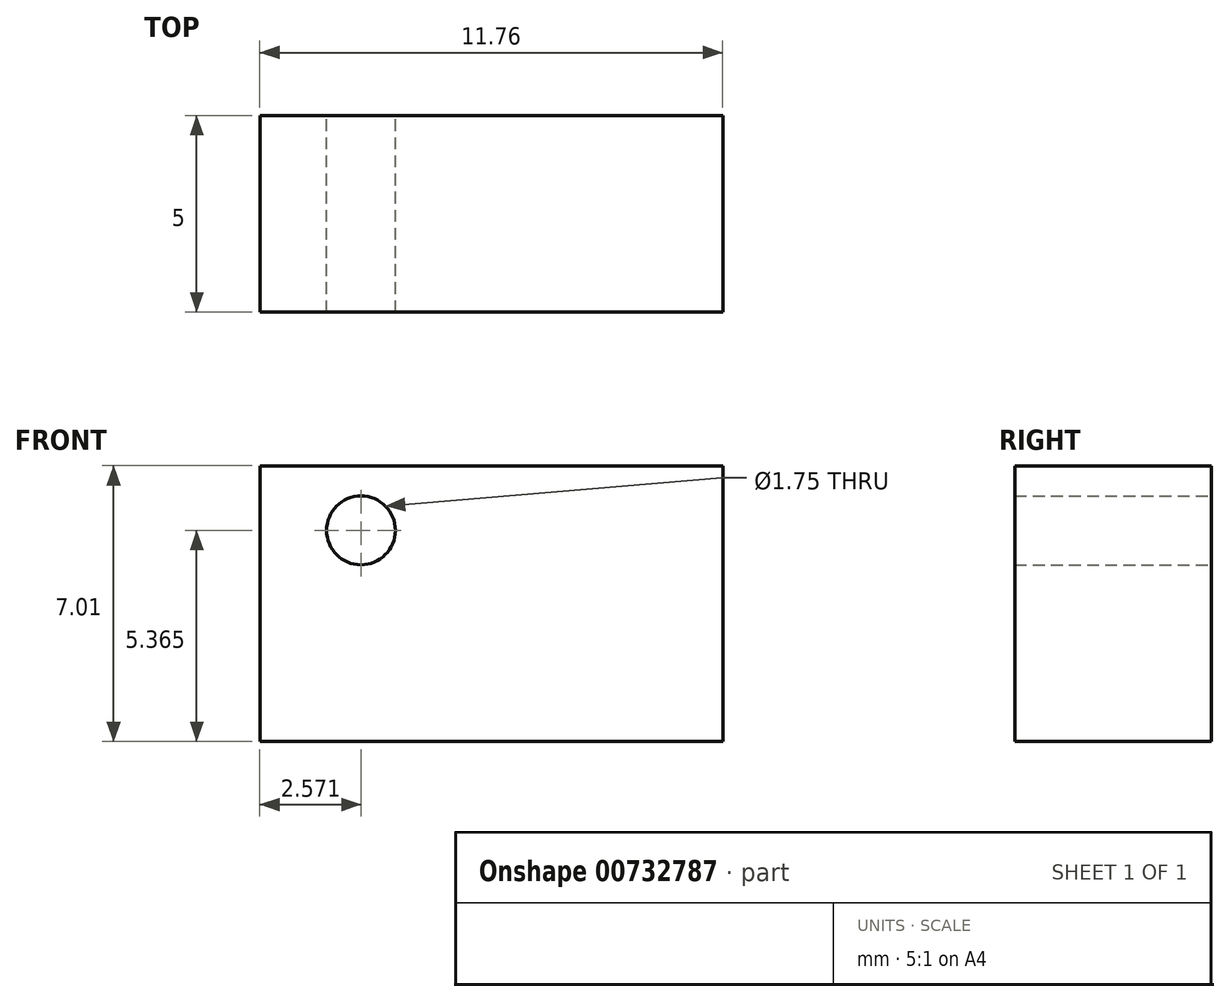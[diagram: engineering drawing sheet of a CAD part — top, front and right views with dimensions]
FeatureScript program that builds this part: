
annotation { "Feature Type Name" : "Feature", "Feature Type Description" : "" }
export const myFeature = defineFeature(function(context is Context, id is Id, definition is map)
    precondition{}
    {
        {
            var Q0;
            Q0=qCreatedBy(makeId("Front.planeOp"),FACE);
            var sketch = newSketch(context, id + "F0", { "sketchPlane" : qUnion([Q0])});
            skLineSegment(sketch, "E0.bottom", {"start": v(-29.15, 29.6) * mm, "end": v(-17.39, 29.6) * mm});
            skLineSegment(sketch, "E0.top", {"start": v(-29.15, 22.6) * mm, "end": v(-17.39, 22.6) * mm});
            skLineSegment(sketch, "E0.left", {"start": v(-29.15, 29.6) * mm, "end": v(-29.15, 22.6) * mm});
            skLineSegment(sketch, "E0.right", {"start": v(-17.39, 29.6) * mm, "end": v(-17.39, 22.6) * mm});
            skLineSegment(sketch, "E1.bottom", {"start": v(-40.74, 0) * mm, "end": v(-30.51, 0) * mm});
            skLineSegment(sketch, "E1.top", {"start": v(-40.74, -8.3) * mm, "end": v(-30.51, -8.3) * mm});
            skLineSegment(sketch, "E1.left", {"start": v(-40.74, 0) * mm, "end": v(-40.74, -8.3) * mm});
            skLineSegment(sketch, "E1.right", {"start": v(-30.51, 0) * mm, "end": v(-30.51, -8.3) * mm});
            skLineSegment(sketch, "E2", {"start": v(-27.8, 31.63) * mm, "end": v(-23.38, 31.63) * mm});
            skLineSegment(sketch, "E3", {"start": v(-23.38, 31.63) * mm, "end": v(-23.15, 30.07) * mm});
            skLineSegment(sketch, "E4", {"start": v(-23.15, 30.07) * mm, "end": v(-27.23, 33.8) * mm});
            skLineSegment(sketch, "E5", {"start": v(-27.23, 33.8) * mm, "end": v(-23.47, 33.8) * mm});
            skLineSegment(sketch, "E6", {"start": v(-23.47, 33.8) * mm, "end": v(-27.8, 31.63) * mm});
            skLineSegment(sketch, "E7", {"start": v(-29.15, 29.6) * mm, "end": v(-27.8, 31.63) * mm});
            skSolve(sketch);
        }
        {
            var Q0;
            Q0=qCreatedBy(makeId("Front.planeOp"),FACE);
            var sketch = newSketch(context, id + "F1", { "sketchPlane" : qUnion([Q0])});
            skCircle(sketch, "E8", {"center": v(-26.58, 27.96) * mm, "radius": 0.87 * mm});
            skCircle(sketch, "E9", {"center": v(-18.8, 27.81) * mm, "radius": 0.5 * mm});
            skCircle(sketch, "E10", {"center": v(-27.25, 24.6) * mm, "radius": 0.7 * mm});
            skCircle(sketch, "E11", {"center": v(-19.41, 24.84) * mm, "radius": 0.63 * mm});
            skSolve(sketch);
        }
        {
            var Q0;
            Q0=makeQuery(id+"F1.imprint","IMPRINT",FACE,{"disambiguationData":[TD([[makeQuery(id+"F1.imprint","IMPRINT",EDGE,{"derivedFrom":sQuery(id+"F1.wireOp",EDGE,"E8")}),1.0]])]});
            var sketch = newSketch(context, id + "F2", { "sketchPlane" : qUnion([Q0])});
            skSolve(sketch);
        }
        {
            var Q0;
            Q0=makeQuery(id+"F0.imprint","IMPRINT",FACE,{"disambiguationData":[TD([[makeQuery(id+"F0.imprint","IMPRINT",EDGE,{"derivedFrom":sQuery(id+"F0.wireOp",EDGE,"E0.bottom")}),-1.0]])]});
            extrude(context, id + "F3", {"entities" : qUnion([Q0]), "depth" : 5 * mm, "offsetDistance" : 25 * mm});
        }
        {
            var Q0;
            Q0=makeQuery(id+"F2.imprint","IMPRINT",FACE,{"disambiguationData":[TD([[makeQuery(id+"F2.imprint","IMPRINT",EDGE,{"derivedFrom":makeQuery(id+"F1.imprint","IMPRINT",EDGE,{"derivedFrom":sQuery(id+"F1.wireOp",EDGE,"E8")})}),1.0]])]});
            extrude(context, id + "F4", {"entities" : qUnion([Q0]), "operationType" : NewBodyOperationType.REMOVE, "depth" : 25 * mm, "offsetDistance" : 25 * mm});
        }
    });
